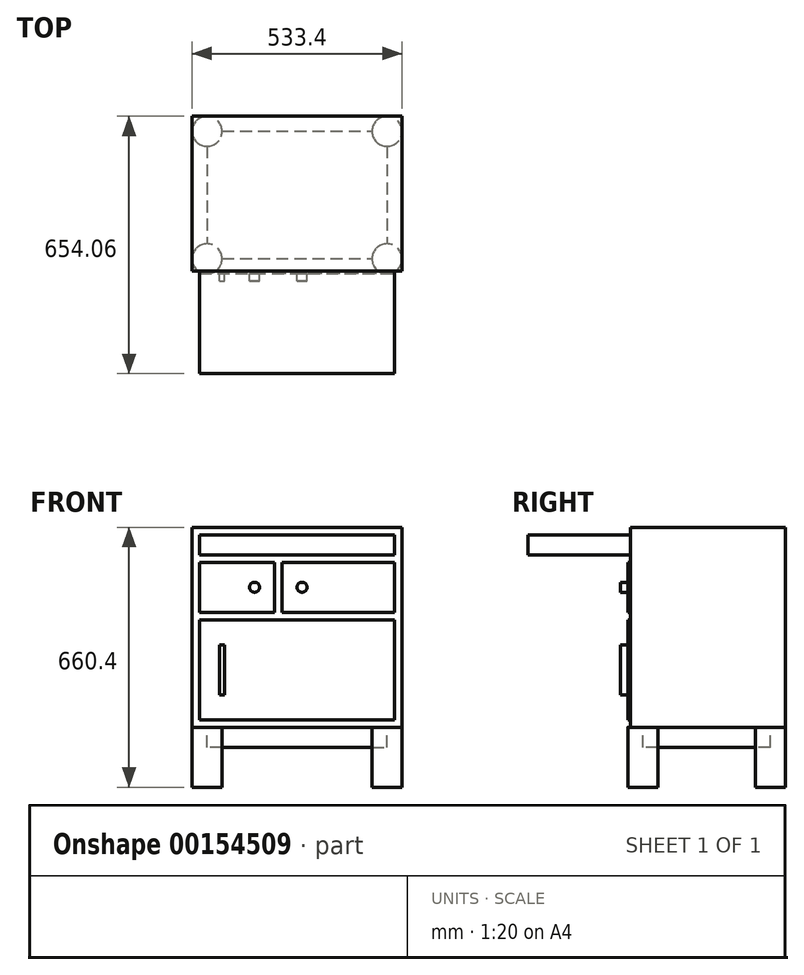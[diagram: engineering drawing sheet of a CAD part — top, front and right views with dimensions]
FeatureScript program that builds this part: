
annotation { "Feature Type Name" : "Feature", "Feature Type Description" : "" }
export const myFeature = defineFeature(function(context is Context, id is Id, definition is map)
    precondition{}
    {
        {
            var Q0;
            Q0=qCreatedBy(makeId("Top.planeOp"),FACE);
            var sketch = newSketch(context, id + "F0", { "sketchPlane" : qUnion([Q0])});
            skLineSegment(sketch, "E0.bottom", {"start": v(266.7, 200.03) * mm, "end": v(-266.7, 200.03) * mm});
            skLineSegment(sketch, "E0.top", {"start": v(266.7, -200.03) * mm, "end": v(-266.7, -200.03) * mm});
            skLineSegment(sketch, "E0.left", {"start": v(266.7, 200.03) * mm, "end": v(266.7, -200.03) * mm});
            skLineSegment(sketch, "E0.right", {"start": v(-266.7, 200.03) * mm, "end": v(-266.7, -200.02) * mm});
            skPoint(sketch, "E0.middle", {"position": v(0, 0) * mm});
            skCircle(sketch, "E1", {"center": v(-228.6, 161.93) * mm, "radius": 38.1 * mm});
            skPoint(sketch, "E1.first.point", {"position": v(-266.7, 161.93) * mm});
            skPoint(sketch, "E1.second.point", {"position": v(-228.6, 200.03) * mm});
            skPoint(sketch, "E1.third.point", {"position": v(-200.97, 135.69) * mm});
            skCircle(sketch, "E2", {"center": v(-228.6, -161.93) * mm, "radius": 38.1 * mm});
            skCircle(sketch, "E3", {"center": v(228.6, -161.93) * mm, "radius": 38.1 * mm});
            skCircle(sketch, "E4", {"center": v(228.6, 161.93) * mm, "radius": 38.1 * mm});
            skLineSegment(sketch, "E5.bottom", {"start": v(-228.6, 161.93) * mm, "end": v(228.6, 161.93) * mm});
            skLineSegment(sketch, "E5.top", {"start": v(-228.6, -161.93) * mm, "end": v(228.6, -161.93) * mm});
            skLineSegment(sketch, "E5.left", {"start": v(-228.6, 161.93) * mm, "end": v(-228.6, -161.93) * mm});
            skLineSegment(sketch, "E5.right", {"start": v(228.6, 161.93) * mm, "end": v(228.6, -161.93) * mm});
            skSolve(sketch);
        }
        {
            var Q0;
            {var subQ0=sQuery(id+"F0.wireOp",EDGE,"E5.bottom");var subQ5=sQuery(id+"F0.wireOp",EDGE,"E1");var subQ6=makeQuery(id+"F0.imprint","INTERSECT",VERTEX,{"derivedFrom":[subQ5,subQ0]});Q0=makeQuery(id+"F0.imprint","IMPRINT",FACE,{"disambiguationData":[TD([[makeQuery(id+"F0.imprint","IMPRINT",EDGE,{"disambiguationData":[TD([[subQ6,1.0]])],"derivedFrom":subQ5}),-1.0]])]});}
            var Q1;
            {var subQ0=sQuery(id+"F0.wireOp",EDGE,"E5.bottom");var subQ1=sQuery(id+"F0.wireOp",EDGE,"E1");var subQ2=makeQuery(id+"F0.imprint","INTERSECT",VERTEX,{"derivedFrom":[subQ1,subQ0]});Q1=makeQuery(id+"F0.imprint","IMPRINT",FACE,{"disambiguationData":[TD([[makeQuery(id+"F0.imprint","IMPRINT",EDGE,{"disambiguationData":[TD([[subQ2,1.0]])],"derivedFrom":subQ1}),1.0]])]});}
            var Q2;
            {var subQ0=sQuery(id+"F0.wireOp",EDGE,"E5.left");var subQ1=sQuery(id+"F0.wireOp",EDGE,"E2");var subQ2=makeQuery(id+"F0.imprint","INTERSECT",VERTEX,{"derivedFrom":[subQ1,subQ0]});Q2=makeQuery(id+"F0.imprint","IMPRINT",FACE,{"disambiguationData":[TD([[makeQuery(id+"F0.imprint","IMPRINT",EDGE,{"disambiguationData":[TD([[subQ2,1.0]])],"derivedFrom":subQ1}),1.0]])]});}
            var Q3;
            {var subQ0=sQuery(id+"F0.wireOp",EDGE,"E5.right");var subQ1=sQuery(id+"F0.wireOp",EDGE,"E3");var subQ2=makeQuery(id+"F0.imprint","INTERSECT",VERTEX,{"derivedFrom":[subQ1,subQ0]});Q3=makeQuery(id+"F0.imprint","IMPRINT",FACE,{"disambiguationData":[TD([[makeQuery(id+"F0.imprint","IMPRINT",EDGE,{"disambiguationData":[TD([[subQ2,-1.0]])],"derivedFrom":subQ1}),1.0]])]});}
            var Q4;
            {var subQ0=sQuery(id+"F0.wireOp",EDGE,"E5.bottom");var subQ1=sQuery(id+"F0.wireOp",EDGE,"E4");var subQ2=makeQuery(id+"F0.imprint","INTERSECT",VERTEX,{"derivedFrom":[subQ1,subQ0]});Q4=makeQuery(id+"F0.imprint","IMPRINT",FACE,{"disambiguationData":[TD([[makeQuery(id+"F0.imprint","IMPRINT",EDGE,{"disambiguationData":[TD([[subQ2,-1.0]])],"derivedFrom":subQ1}),1.0]])]});}
            extrude(context, id + "F1", {"entities" : qUnion([Q0, Q1, Q2, Q3, Q4]), "oppositeDirection" : true, "depth" : 50.8 * mm});
        }
        {
            var Q0;
            {var subQ3=sQuery(id+"F0.wireOp",EDGE,"E2");var subQ5=makeQuery(id+"F0.imprint","INTERSECT",VERTEX,{"derivedFrom":[sQuery(id+"F0.wireOp",EDGE,"E0.right"),subQ3]});Q0=makeQuery(id+"F0.imprint","IMPRINT",FACE,{"disambiguationData":[TD([[makeQuery(id+"F0.imprint","IMPRINT",EDGE,{"disambiguationData":[TD([[subQ5,1.0]])],"derivedFrom":subQ3}),1.0]])]});}
            var Q1;
            {var subQ0=sQuery(id+"F0.wireOp",EDGE,"E5.left");var subQ1=sQuery(id+"F0.wireOp",EDGE,"E2");var subQ2=makeQuery(id+"F0.imprint","INTERSECT",VERTEX,{"derivedFrom":[subQ1,subQ0]});Q1=makeQuery(id+"F0.imprint","IMPRINT",FACE,{"disambiguationData":[TD([[makeQuery(id+"F0.imprint","IMPRINT",EDGE,{"disambiguationData":[TD([[subQ2,1.0]])],"derivedFrom":subQ1}),1.0]])]});}
            var Q2;
            {var subQ0=sQuery(id+"F0.wireOp",EDGE,"E5.bottom");var subQ1=sQuery(id+"F0.wireOp",EDGE,"E1");var subQ2=makeQuery(id+"F0.imprint","INTERSECT",VERTEX,{"derivedFrom":[subQ1,subQ0]});Q2=makeQuery(id+"F0.imprint","IMPRINT",FACE,{"disambiguationData":[TD([[makeQuery(id+"F0.imprint","IMPRINT",EDGE,{"disambiguationData":[TD([[subQ2,1.0]])],"derivedFrom":subQ1}),1.0]])]});}
            var Q3;
            {var subQ3=sQuery(id+"F0.wireOp",EDGE,"E1");var subQ7=makeQuery(id+"F0.imprint","INTERSECT",VERTEX,{"derivedFrom":[sQuery(id+"F0.wireOp",EDGE,"E0.bottom"),subQ3]});Q3=makeQuery(id+"F0.imprint","IMPRINT",FACE,{"disambiguationData":[TD([[makeQuery(id+"F0.imprint","IMPRINT",EDGE,{"disambiguationData":[TD([[subQ7,1.0]])],"derivedFrom":subQ3}),1.0]])]});}
            var Q4;
            {var subQ0=sQuery(id+"F0.wireOp",EDGE,"E5.bottom");var subQ1=sQuery(id+"F0.wireOp",EDGE,"E4");var subQ2=makeQuery(id+"F0.imprint","INTERSECT",VERTEX,{"derivedFrom":[subQ1,subQ0]});Q4=makeQuery(id+"F0.imprint","IMPRINT",FACE,{"disambiguationData":[TD([[makeQuery(id+"F0.imprint","IMPRINT",EDGE,{"disambiguationData":[TD([[subQ2,-1.0]])],"derivedFrom":subQ1}),1.0]])]});}
            var Q5;
            {var subQ3=sQuery(id+"F0.wireOp",EDGE,"E4");var subQ7=makeQuery(id+"F0.imprint","INTERSECT",VERTEX,{"derivedFrom":[sQuery(id+"F0.wireOp",EDGE,"E0.bottom"),subQ3]});Q5=makeQuery(id+"F0.imprint","IMPRINT",FACE,{"disambiguationData":[TD([[makeQuery(id+"F0.imprint","IMPRINT",EDGE,{"disambiguationData":[TD([[subQ7,1.0]])],"derivedFrom":subQ3}),1.0]])]});}
            var Q6;
            {var subQ0=sQuery(id+"F0.wireOp",EDGE,"E5.right");var subQ1=sQuery(id+"F0.wireOp",EDGE,"E3");var subQ2=makeQuery(id+"F0.imprint","INTERSECT",VERTEX,{"derivedFrom":[subQ1,subQ0]});Q6=makeQuery(id+"F0.imprint","IMPRINT",FACE,{"disambiguationData":[TD([[makeQuery(id+"F0.imprint","IMPRINT",EDGE,{"disambiguationData":[TD([[subQ2,-1.0]])],"derivedFrom":subQ1}),1.0]])]});}
            var Q7;
            {var subQ3=sQuery(id+"F0.wireOp",EDGE,"E3");var subQ6=makeQuery(id+"F0.imprint","INTERSECT",VERTEX,{"derivedFrom":[sQuery(id+"F0.wireOp",EDGE,"E0.left"),subQ3]});Q7=makeQuery(id+"F0.imprint","IMPRINT",FACE,{"disambiguationData":[TD([[makeQuery(id+"F0.imprint","IMPRINT",EDGE,{"disambiguationData":[TD([[subQ6,-1.0]])],"derivedFrom":subQ3}),1.0]])]});}
            extrude(context, id + "F2", {"entities" : qUnion([Q0, Q1, Q2, Q3, Q4, Q5, Q6, Q7]), "operationType" : NewBodyOperationType.ADD, "oppositeDirection" : true, "depth" : 152.4 * mm});
        }
        {
            var Q0;
            {var subQ0=sQuery(id+"F0.wireOp",EDGE,"E1");var subQ1=sQuery(id+"F0.wireOp",EDGE,"E0.right");var subQ2=makeQuery(id+"F0.imprint","INTERSECT",VERTEX,{"derivedFrom":[subQ1,subQ0]});Q0=makeQuery(id+"F0.imprint","IMPRINT",FACE,{"disambiguationData":[TD([[makeQuery(id+"F0.imprint","IMPRINT",EDGE,{"disambiguationData":[TD([[subQ2,-1.0]])],"derivedFrom":subQ1}),1.0]])]});}
            var Q1;
            {var subQ0=sQuery(id+"F0.wireOp",EDGE,"E0.right");var subQ1=sQuery(id+"F0.wireOp",EDGE,"E0.bottom");var subQ2=makeQuery(id+"F0.imprint","INTERSECT",VERTEX,{"derivedFrom":[subQ1,subQ0]});Q1=makeQuery(id+"F0.imprint","IMPRINT",FACE,{"disambiguationData":[TD([[makeQuery(id+"F0.imprint","IMPRINT",EDGE,{"disambiguationData":[TD([[subQ2,1.0]])],"derivedFrom":subQ1}),1.0]])]});}
            var Q2;
            {var subQ3=sQuery(id+"F0.wireOp",EDGE,"E1");var subQ7=makeQuery(id+"F0.imprint","INTERSECT",VERTEX,{"derivedFrom":[sQuery(id+"F0.wireOp",EDGE,"E0.bottom"),subQ3]});Q2=makeQuery(id+"F0.imprint","IMPRINT",FACE,{"disambiguationData":[TD([[makeQuery(id+"F0.imprint","IMPRINT",EDGE,{"disambiguationData":[TD([[subQ7,1.0]])],"derivedFrom":subQ3}),1.0]])]});}
            var Q3;
            {var subQ0=sQuery(id+"F0.wireOp",EDGE,"E5.bottom");var subQ1=sQuery(id+"F0.wireOp",EDGE,"E1");var subQ2=makeQuery(id+"F0.imprint","INTERSECT",VERTEX,{"derivedFrom":[subQ1,subQ0]});Q3=makeQuery(id+"F0.imprint","IMPRINT",FACE,{"disambiguationData":[TD([[makeQuery(id+"F0.imprint","IMPRINT",EDGE,{"disambiguationData":[TD([[subQ2,1.0]])],"derivedFrom":subQ1}),1.0]])]});}
            var Q4;
            {var subQ0=sQuery(id+"F0.wireOp",EDGE,"E5.bottom");var subQ5=sQuery(id+"F0.wireOp",EDGE,"E1");var subQ6=makeQuery(id+"F0.imprint","INTERSECT",VERTEX,{"derivedFrom":[subQ5,subQ0]});Q4=makeQuery(id+"F0.imprint","IMPRINT",FACE,{"disambiguationData":[TD([[makeQuery(id+"F0.imprint","IMPRINT",EDGE,{"disambiguationData":[TD([[subQ6,1.0]])],"derivedFrom":subQ5}),-1.0]])]});}
            var Q5;
            {var subQ0=sQuery(id+"F0.wireOp",EDGE,"E5.left");var subQ1=sQuery(id+"F0.wireOp",EDGE,"E2");var subQ2=makeQuery(id+"F0.imprint","INTERSECT",VERTEX,{"derivedFrom":[subQ1,subQ0]});Q5=makeQuery(id+"F0.imprint","IMPRINT",FACE,{"disambiguationData":[TD([[makeQuery(id+"F0.imprint","IMPRINT",EDGE,{"disambiguationData":[TD([[subQ2,1.0]])],"derivedFrom":subQ1}),1.0]])]});}
            var Q6;
            {var subQ3=sQuery(id+"F0.wireOp",EDGE,"E2");var subQ5=makeQuery(id+"F0.imprint","INTERSECT",VERTEX,{"derivedFrom":[sQuery(id+"F0.wireOp",EDGE,"E0.right"),subQ3]});Q6=makeQuery(id+"F0.imprint","IMPRINT",FACE,{"disambiguationData":[TD([[makeQuery(id+"F0.imprint","IMPRINT",EDGE,{"disambiguationData":[TD([[subQ5,1.0]])],"derivedFrom":subQ3}),1.0]])]});}
            var Q7;
            {var subQ0=sQuery(id+"F0.wireOp",EDGE,"E0.right");var subQ1=sQuery(id+"F0.wireOp",EDGE,"E0.top");var subQ2=makeQuery(id+"F0.imprint","INTERSECT",VERTEX,{"derivedFrom":[subQ1,subQ0]});Q7=makeQuery(id+"F0.imprint","IMPRINT",FACE,{"disambiguationData":[TD([[makeQuery(id+"F0.imprint","IMPRINT",EDGE,{"disambiguationData":[TD([[subQ2,1.0]])],"derivedFrom":subQ1}),-1.0]])]});}
            var Q8;
            {var subQ0=sQuery(id+"F0.wireOp",EDGE,"E3");var subQ1=sQuery(id+"F0.wireOp",EDGE,"E0.top");var subQ2=makeQuery(id+"F0.imprint","INTERSECT",VERTEX,{"derivedFrom":[subQ1,subQ0]});Q8=makeQuery(id+"F0.imprint","IMPRINT",FACE,{"disambiguationData":[TD([[makeQuery(id+"F0.imprint","IMPRINT",EDGE,{"disambiguationData":[TD([[subQ2,-1.0]])],"derivedFrom":subQ1}),-1.0]])]});}
            var Q9;
            {var subQ3=sQuery(id+"F0.wireOp",EDGE,"E3");var subQ6=makeQuery(id+"F0.imprint","INTERSECT",VERTEX,{"derivedFrom":[sQuery(id+"F0.wireOp",EDGE,"E0.left"),subQ3]});Q9=makeQuery(id+"F0.imprint","IMPRINT",FACE,{"disambiguationData":[TD([[makeQuery(id+"F0.imprint","IMPRINT",EDGE,{"disambiguationData":[TD([[subQ6,-1.0]])],"derivedFrom":subQ3}),1.0]])]});}
            var Q10;
            {var subQ0=sQuery(id+"F0.wireOp",EDGE,"E0.left");var subQ1=sQuery(id+"F0.wireOp",EDGE,"E0.top");var subQ2=makeQuery(id+"F0.imprint","INTERSECT",VERTEX,{"derivedFrom":[subQ1,subQ0]});Q10=makeQuery(id+"F0.imprint","IMPRINT",FACE,{"disambiguationData":[TD([[makeQuery(id+"F0.imprint","IMPRINT",EDGE,{"disambiguationData":[TD([[subQ2,-1.0]])],"derivedFrom":subQ1}),-1.0]])]});}
            var Q11;
            {var subQ0=sQuery(id+"F0.wireOp",EDGE,"E5.right");var subQ1=sQuery(id+"F0.wireOp",EDGE,"E3");var subQ2=makeQuery(id+"F0.imprint","INTERSECT",VERTEX,{"derivedFrom":[subQ1,subQ0]});Q11=makeQuery(id+"F0.imprint","IMPRINT",FACE,{"disambiguationData":[TD([[makeQuery(id+"F0.imprint","IMPRINT",EDGE,{"disambiguationData":[TD([[subQ2,-1.0]])],"derivedFrom":subQ1}),1.0]])]});}
            var Q12;
            {var subQ0=sQuery(id+"F0.wireOp",EDGE,"E4");var subQ1=sQuery(id+"F0.wireOp",EDGE,"E0.left");var subQ2=makeQuery(id+"F0.imprint","INTERSECT",VERTEX,{"derivedFrom":[subQ1,subQ0]});Q12=makeQuery(id+"F0.imprint","IMPRINT",FACE,{"disambiguationData":[TD([[makeQuery(id+"F0.imprint","IMPRINT",EDGE,{"disambiguationData":[TD([[subQ2,-1.0]])],"derivedFrom":subQ1}),-1.0]])]});}
            var Q13;
            {var subQ0=sQuery(id+"F0.wireOp",EDGE,"E4");var subQ1=sQuery(id+"F0.wireOp",EDGE,"E0.bottom");var subQ2=makeQuery(id+"F0.imprint","INTERSECT",VERTEX,{"derivedFrom":[subQ1,subQ0]});Q13=makeQuery(id+"F0.imprint","IMPRINT",FACE,{"disambiguationData":[TD([[makeQuery(id+"F0.imprint","IMPRINT",EDGE,{"disambiguationData":[TD([[subQ2,-1.0]])],"derivedFrom":subQ1}),1.0]])]});}
            var Q14;
            {var subQ0=sQuery(id+"F0.wireOp",EDGE,"E0.left");var subQ1=sQuery(id+"F0.wireOp",EDGE,"E0.bottom");var subQ2=makeQuery(id+"F0.imprint","INTERSECT",VERTEX,{"derivedFrom":[subQ1,subQ0]});Q14=makeQuery(id+"F0.imprint","IMPRINT",FACE,{"disambiguationData":[TD([[makeQuery(id+"F0.imprint","IMPRINT",EDGE,{"disambiguationData":[TD([[subQ2,-1.0]])],"derivedFrom":subQ1}),1.0]])]});}
            var Q15;
            {var subQ3=sQuery(id+"F0.wireOp",EDGE,"E4");var subQ7=makeQuery(id+"F0.imprint","INTERSECT",VERTEX,{"derivedFrom":[sQuery(id+"F0.wireOp",EDGE,"E0.bottom"),subQ3]});Q15=makeQuery(id+"F0.imprint","IMPRINT",FACE,{"disambiguationData":[TD([[makeQuery(id+"F0.imprint","IMPRINT",EDGE,{"disambiguationData":[TD([[subQ7,1.0]])],"derivedFrom":subQ3}),1.0]])]});}
            var Q16;
            {var subQ0=sQuery(id+"F0.wireOp",EDGE,"E5.bottom");var subQ1=sQuery(id+"F0.wireOp",EDGE,"E4");var subQ2=makeQuery(id+"F0.imprint","INTERSECT",VERTEX,{"derivedFrom":[subQ1,subQ0]});Q16=makeQuery(id+"F0.imprint","IMPRINT",FACE,{"disambiguationData":[TD([[makeQuery(id+"F0.imprint","IMPRINT",EDGE,{"disambiguationData":[TD([[subQ2,-1.0]])],"derivedFrom":subQ1}),1.0]])]});}
            extrude(context, id + "F3", {"entities" : qUnion([Q0, Q1, Q2, Q3, Q4, Q5, Q6, Q7, Q8, Q9, Q10, Q11, Q12, Q13, Q14, Q15, Q16]), "operationType" : NewBodyOperationType.ADD, "depth" : 508 * mm});
        }
        {
            var Q0;
            Q0=makeQuery(id+"F3.opExtrude","SWEPT_FACE",FACE,{"disambiguationData":[OSD([sQuery(id+"F0.wireOp",EDGE,"E0.top")])]});
            var sketch = newSketch(context, id + "F4", { "sketchPlane" : qUnion([Q0])});
            skLineSegment(sketch, "E6.bottom", {"start": v(-247.65, 488.95) * mm, "end": v(247.65, 488.95) * mm});
            skLineSegment(sketch, "E6.top", {"start": v(-247.65, 438.15) * mm, "end": v(247.65, 438.15) * mm});
            skLineSegment(sketch, "E6.left", {"start": v(-247.65, 488.95) * mm, "end": v(-247.65, 438.15) * mm});
            skLineSegment(sketch, "E6.right", {"start": v(247.65, 488.95) * mm, "end": v(247.65, 438.15) * mm});
            skLineSegment(sketch, "E7.bottom", {"start": v(-247.65, 419.1) * mm, "end": v(-57.15, 419.1) * mm});
            skLineSegment(sketch, "E7.top", {"start": v(-247.65, 292.1) * mm, "end": v(-57.15, 292.1) * mm});
            skLineSegment(sketch, "E7.left", {"start": v(-247.65, 419.1) * mm, "end": v(-247.65, 292.1) * mm});
            skLineSegment(sketch, "E7.right", {"start": v(-57.15, 419.1) * mm, "end": v(-57.15, 292.1) * mm});
            skLineSegment(sketch, "E8.bottom", {"start": v(247.65, 419.1) * mm, "end": v(-38.1, 419.1) * mm});
            skLineSegment(sketch, "E8.top", {"start": v(247.65, 292.1) * mm, "end": v(-38.1, 292.1) * mm});
            skLineSegment(sketch, "E8.left", {"start": v(247.65, 419.1) * mm, "end": v(247.65, 292.1) * mm});
            skLineSegment(sketch, "E8.right", {"start": v(-38.1, 419.1) * mm, "end": v(-38.1, 292.1) * mm});
            skLineSegment(sketch, "E9.bottom", {"start": v(-247.65, 273.05) * mm, "end": v(247.65, 273.05) * mm});
            skLineSegment(sketch, "E9.top", {"start": v(-247.65, 19.05) * mm, "end": v(247.65, 19.05) * mm});
            skLineSegment(sketch, "E9.left", {"start": v(-247.65, 273.05) * mm, "end": v(-247.65, 19.05) * mm});
            skLineSegment(sketch, "E9.right", {"start": v(247.65, 273.05) * mm, "end": v(247.65, 19.05) * mm});
            skCircle(sketch, "E10", {"center": v(-107.95, 355.6) * mm, "radius": 12.7 * mm});
            skCircle(sketch, "E11", {"center": v(12.7, 355.6) * mm, "radius": 12.7 * mm});
            skLineSegment(sketch, "E12.bottom", {"start": v(-196.85, 209.55) * mm, "end": v(-184.15, 209.55) * mm});
            skLineSegment(sketch, "E12.top", {"start": v(-196.85, 82.55) * mm, "end": v(-184.15, 82.55) * mm});
            skLineSegment(sketch, "E12.left", {"start": v(-196.85, 209.55) * mm, "end": v(-196.85, 82.55) * mm});
            skLineSegment(sketch, "E12.right", {"start": v(-184.15, 209.55) * mm, "end": v(-184.15, 82.55) * mm});
            skLineSegment(sketch, "E13", {"start": v(-57.15, 355.6) * mm, "end": v(-107.95, 355.6) * mm, "construction": true});
            skLineSegment(sketch, "E14", {"start": v(12.7, 355.6) * mm, "end": v(-38.1, 355.6) * mm, "construction": true});
            skLineSegment(sketch, "E15", {"start": v(-196.85, 146.05) * mm, "end": v(-247.65, 146.05) * mm, "construction": true});
            skLineSegment(sketch, "E16.bottom", {"start": v(-266.7, 508) * mm, "end": v(266.7, 508) * mm});
            skLineSegment(sketch, "E16.top", {"start": v(-266.7, 0) * mm, "end": v(266.7, 0) * mm});
            skLineSegment(sketch, "E16.left", {"start": v(-266.7, 508) * mm, "end": v(-266.7, 0) * mm});
            skLineSegment(sketch, "E16.right", {"start": v(266.7, 508) * mm, "end": v(266.7, 0) * mm});
            skSolve(sketch);
        }
        {
            var Q0;
            Q0=makeQuery(id+"F4.imprint","IMPRINT",FACE,{"disambiguationData":[TD([[makeQuery(id+"F4.imprint","IMPRINT",EDGE,{"derivedFrom":sQuery(id+"F4.wireOp",EDGE,"E6.bottom")}),1.0]])]});
            extrude(context, id + "F5", {"entities" : qUnion([Q0]), "operationType" : NewBodyOperationType.REMOVE, "oppositeDirection" : true, "depth" : 6.35 * mm});
        }
        {
            var Q0;
            Q0=makeQuery(id+"F4.imprint","IMPRINT",FACE,{"disambiguationData":[TD([[makeQuery(id+"F4.imprint","IMPRINT",EDGE,{"derivedFrom":sQuery(id+"F4.wireOp",EDGE,"E6.bottom")}),-1.0]])]});
            extrude(context, id + "F6", {"entities" : qUnion([Q0]), "operationType" : NewBodyOperationType.ADD, "depth" : 254 * mm});
        }
        {
            var Q0;
            Q0=makeQuery(id+"F4.imprint","IMPRINT",FACE,{"disambiguationData":[TD([[makeQuery(id+"F4.imprint","IMPRINT",EDGE,{"derivedFrom":sQuery(id+"F4.wireOp",EDGE,"E12.bottom")}),-1.0]])]});
            var Q1;
            Q1=makeQuery(id+"F4.imprint","IMPRINT",FACE,{"disambiguationData":[TD([[makeQuery(id+"F4.imprint","IMPRINT",EDGE,{"derivedFrom":sQuery(id+"F4.wireOp",EDGE,"E10")}),1.0]])]});
            var Q2;
            Q2=makeQuery(id+"F4.imprint","IMPRINT",FACE,{"disambiguationData":[TD([[makeQuery(id+"F4.imprint","IMPRINT",EDGE,{"derivedFrom":sQuery(id+"F4.wireOp",EDGE,"E11")}),1.0]])]});
            extrude(context, id + "F7", {"entities" : qUnion([Q0, Q1, Q2]), "operationType" : NewBodyOperationType.ADD, "depth" : 19.05 * mm});
        }
    });
